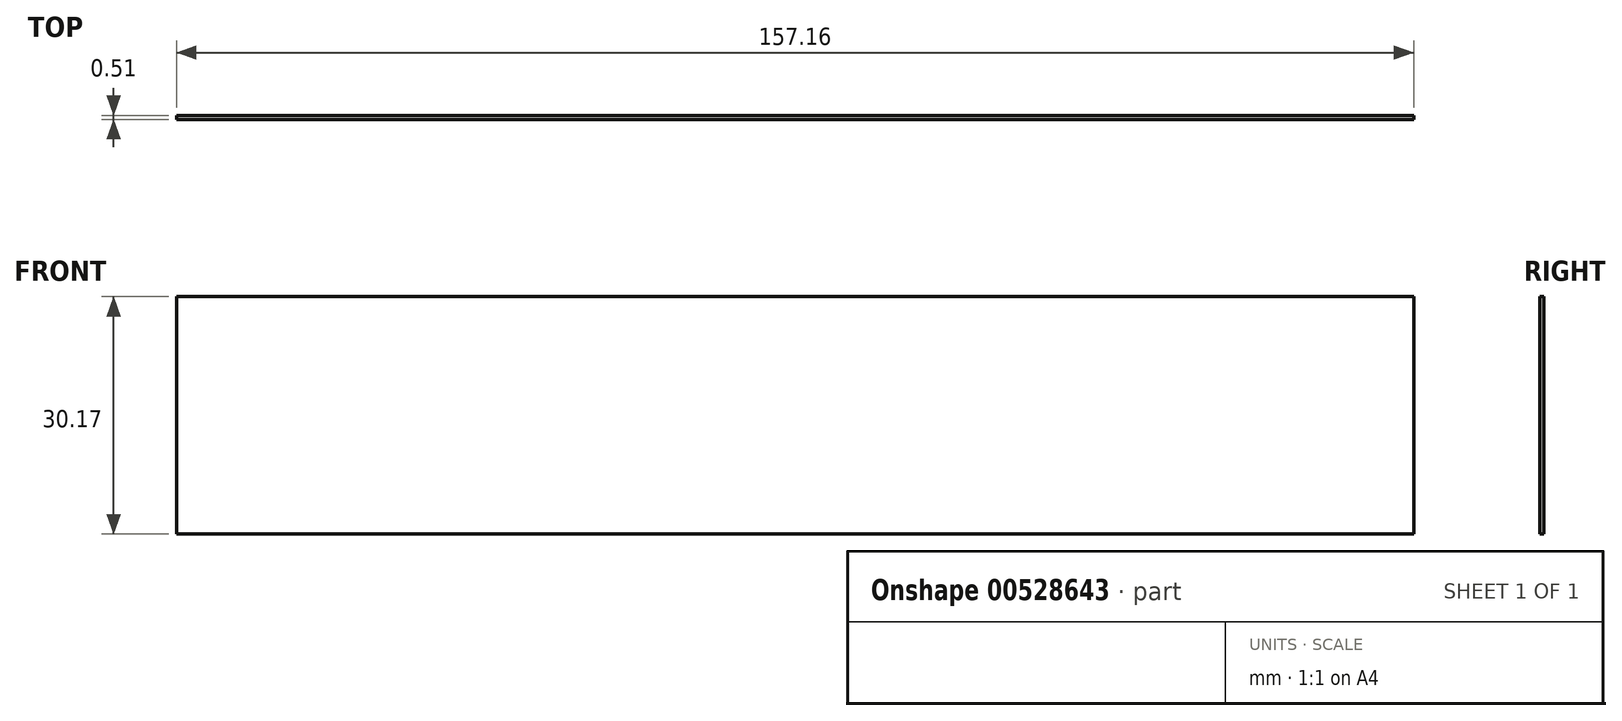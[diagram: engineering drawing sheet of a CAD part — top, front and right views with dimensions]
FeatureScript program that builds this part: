
annotation { "Feature Type Name" : "Feature", "Feature Type Description" : "" }
export const myFeature = defineFeature(function(context is Context, id is Id, definition is map)
    precondition{}
    {
        {
            var Q0;
            Q0=qCreatedBy(makeId("Front.planeOp"),FACE);
            var sketch = newSketch(context, id + "F0", { "sketchPlane" : qUnion([Q0])});
            skLineSegment(sketch, "E0", {"start": v(-79.41, 22.58) * mm, "end": v(77.75, 22.58) * mm});
            skLineSegment(sketch, "E1", {"start": v(-79.41, 22.58) * mm, "end": v(-79.41, -7.58) * mm});
            skLineSegment(sketch, "E2", {"start": v(77.75, 22.58) * mm, "end": v(77.75, -7.58) * mm});
            skLineSegment(sketch, "E3", {"start": v(-79.41, -7.58) * mm, "end": v(77.75, -7.58) * mm});
            skSolve(sketch);
        }
        {
            var Q0;
            Q0 = qSketchRegion(id + "F0", true);
            var Q1;
            Q1=sQuery(id+"F0.wireOp",EDGE,"E0");
            var Q2;
            Q2=sQuery(id+"F0.wireOp",EDGE,"E1");
            var Q3;
            Q3=sQuery(id+"F0.wireOp",EDGE,"E3");
            var Q4;
            Q4=sQuery(id+"F0.wireOp",EDGE,"E2");
            extrude(context, id + "F1", {"entities" : qUnion([Q0]), "bodyType" : ToolBodyType.SURFACE, "surfaceEntities" : qUnion([Q1, Q2, Q3, Q4]), "depth" : 4.76 * mm, "offsetDistance" : 25.4 * mm});
        }
        {
            var Q0;
            Q0=qCreatedBy(makeId("Front.planeOp"),FACE);
            var sketch = newSketch(context, id + "F2", { "sketchPlane" : qUnion([Q0])});
            skLineSegment(sketch, "E4.bottom", {"start": v(-79.41, 22.57) * mm, "end": v(77.75, 22.57) * mm});
            skLineSegment(sketch, "E4.top", {"start": v(-79.41, -7.6) * mm, "end": v(77.75, -7.6) * mm});
            skLineSegment(sketch, "E4.left", {"start": v(-79.41, 22.57) * mm, "end": v(-79.41, -7.6) * mm});
            skLineSegment(sketch, "E4.right", {"start": v(77.75, 22.57) * mm, "end": v(77.75, -7.6) * mm});
            skSolve(sketch);
        }
        {
            var Q0;
            Q0 = qSketchRegion(id + "F2", true);
            extrude(context, id + "F3", {"entities" : qUnion([Q0]), "depth" : 0.5 * mm, "offsetDistance" : 25.4 * mm});
        }
        {
            var Q0;
            Q0=qCreatedBy(makeId("Front.planeOp"),FACE);
            var sketch = newSketch(context, id + "F4", { "sketchPlane" : qUnion([Q0])});
            skLineSegment(sketch, "E5", {"start": v(-19.08, 22.51) * mm, "end": v(29.29, 22.51) * mm});
            skLineSegment(sketch, "E6.0", {"start": v(-19.08, -7.65) * mm, "end": v(29.29, -7.65) * mm});
            skSolve(sketch);
        }
        {
            var Q0;
            Q0 = qSketchRegion(id + "F4", true);
            var Q1;
            Q1=sQuery(id+"F4.wireOp",EDGE,"E5");
            var Q2;
            Q2=sQuery(id+"F4.wireOp",EDGE,"E6.0");
            extrude(context, id + "F5", {"entities" : qUnion([Q0]), "bodyType" : ToolBodyType.SURFACE, "surfaceEntities" : qUnion([Q1, Q2]), "depth" : 17.48 * mm, "offsetDistance" : 25.4 * mm});
        }
    });
